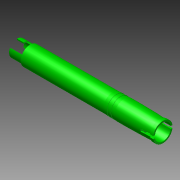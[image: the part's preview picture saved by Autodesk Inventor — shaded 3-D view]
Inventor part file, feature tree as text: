
AUTODESK INVENTOR PART (.ipt)
format: ipt  version: 2015 (Build 190159000, 159)  size: 306,176 bytes
history: native  units: in
note: dims shown in document units (in); Inventor stores cm internally (conversion verified against a paired STEP export)
features: extrude x10, sketch x10, revolve x3, hole x2, plane x2, mirror x1, pattern_circular x1, chamfer x1
ambient origin geometry x8: Origin, YZ Plane, XZ Plane, XY Plane, X Axis, Y Axis, Z Axis, Center Point
bodies: Solid1 (feature_tree)
feature tree (30):
  revolve  "Revolution1"  [1 undecoded]
  extrude  "Extrusion1"  Depth=0.29in
  hole  "Hole1"  [1 undecoded]
  hole  "Hole2"  [1 undecoded]
  sketch  "Sketch3"  dims[d4=0.3in d5=0.1in]
  extrude  "Extrusion2"  Depth=0.3in
  extrude  "Extrusion3"  Depth=0.05in
  extrude  "Extrusion4"  Depth=0.04in
  mirror  "Mirror1"
  plane  "Work Plane2"
  sketch  "Sketch7"  dims[d8=0.3in d9=0.44in]
  extrude  "Extrusion5"  Depth=0.2in TaperAngle=0.0deg
  extrude  "Extrusion6"  Depth=0.125in
  pattern_circular  "Circular Pattern1"  [2 undecoded]
  plane  "Work Plane3"
  extrude  "Extrusion7"  Depth=0.125in TaperAngle=0.0deg
  sketch  "Sketch9"  dims[d12=90.0deg d13=0.04in]
  extrude  "Extrusion8"  Depth=0.125in TaperAngle=0.0deg
  extrude  "Extrusion9"  [1 undecoded]
  revolve  "Revolution2"  [1 undecoded]
  revolve  "Revolution3"  [1 undecoded]
  extrude  "Extrusion10"  Depth=0.125in
  chamfer  "Chamfer1"  Distance=0.01in
  sketch  "Sketch1"  dims[d0=0.07in d1=0.4in]
  sketch  "Sketch2"  dims[d2=0.365in d3=0.29in]
  sketch  "Sketch4"  dims[d6=0.06in d7=0.3in]
  sketch  "Sketch8"  dims[d10=0.28in d11=0.05in]
  sketch  "Sketch10"  dims[d14=0.2in d15=1.0in d16=0.0in]
  sketch  "Sketch11"  dims[d17=1.0in d18=1.0in]
  sketch  "Sketch12"  dims[d19=0.1875in d20=0.75in d21=0.25in d22=0.25in d23=0.5635in d24=0.4375in d25=0.0in d26=1.0in d27=1.0in d28=0.1875in d29=0.75in d30=0.25in d31=0.05in d32=0.5635in d33=0.375in d34=0.0in d35=0.07in d36=0.0in d37=0.085in d38=0.0in d39=1.15in d40=0.0in d42=-1.44in d43=0.45in d44=0.025in d45=0.025in d46=0.01in d47=0.03in d48=0.05in d49=0.0in d50=0.05in d51=0.0in d52=5.1181in d53=360.0deg d55=-1.8in d56=1.8in d57=0.0in d58=0.02in d59=0.4in d60=0.0in d61=0.2in d62=0.0in d63=0.2in d64=0.4466in d65=0.1in d66=30.0deg d67=0.0053in d68=0.0053in d69=0.0053in d70=0.0in d71=0.0053in d72=0.125in d73=45.0deg]
note: 8 required parameter values undecoded (feature->parameter linkage not recoverable at this tier; creation-order binding heuristic only, values carry confidence <= 0.55)